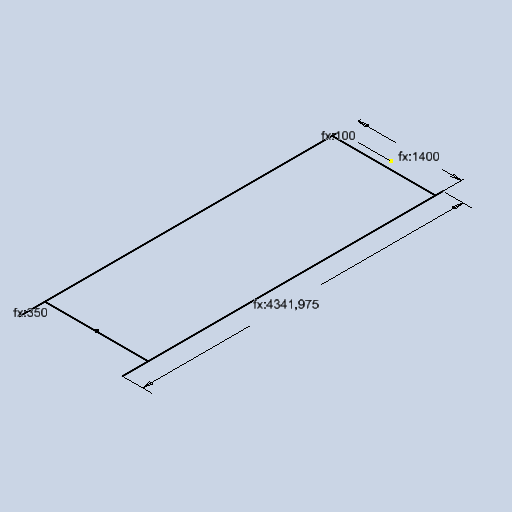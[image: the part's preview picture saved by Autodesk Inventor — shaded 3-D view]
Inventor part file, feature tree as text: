
AUTODESK INVENTOR PART (.ipt)
format: ipt  version: 2025 (Build 290162010, 162A)  size: 86,016 bytes
history: native  units: in
note: dims shown in document units (in); Inventor stores cm internally (conversion verified against a paired STEP export)
features: sketch x1
ambient origin geometry x8: Origin, YZ Plane, XZ Plane, XY Plane, X Axis, Y Axis, Z Axis, Center Point
feature tree (1):
  sketch  "Sketch3"  dims[d7=170.9439in d8=3.937in d9=13.7795in d10=55.1181in]
